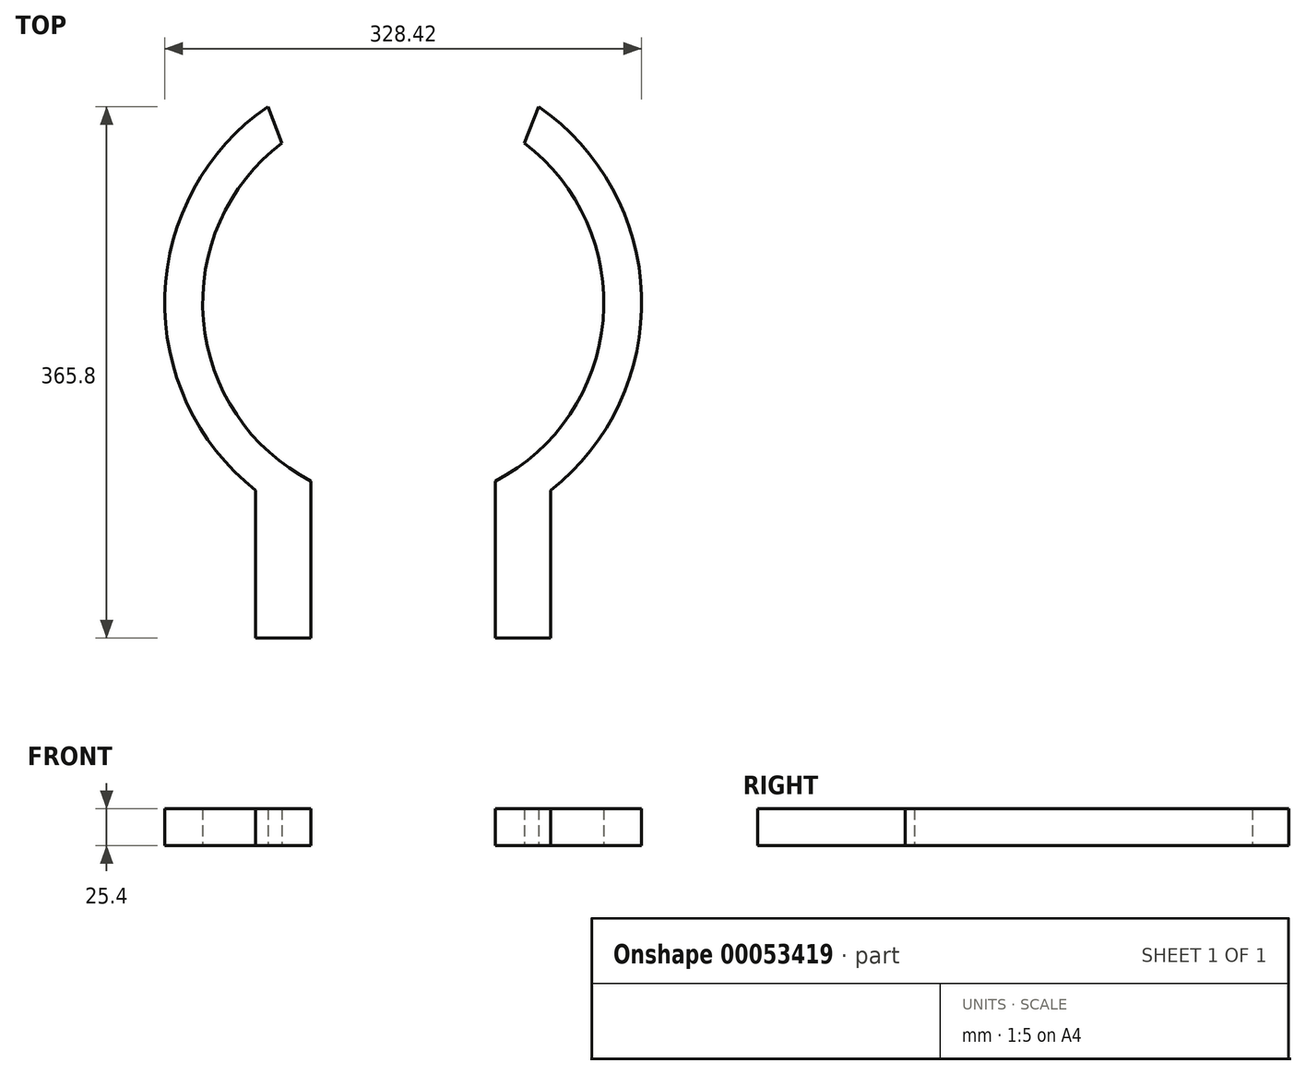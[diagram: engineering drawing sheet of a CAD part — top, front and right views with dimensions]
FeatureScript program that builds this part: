
annotation { "Feature Type Name" : "Feature", "Feature Type Description" : "" }
export const myFeature = defineFeature(function(context is Context, id is Id, definition is map)
    precondition{}
    {
        {
            var Q0;
            Q0=qCreatedBy(makeId("Top.planeOp"),FACE);
            var sketch = newSketch(context, id + "F0", { "sketchPlane" : qUnion([Q0])});
            skLineSegment(sketch, "E0", {"start": v(-63.5, -122.65) * mm, "end": v(-63.5, -230.6) * mm});
            skLineSegment(sketch, "E1", {"start": v(-63.5, -230.6) * mm, "end": v(-101.6, -230.6) * mm});
            skLineSegment(sketch, "E2", {"start": v(-101.6, -230.6) * mm, "end": v(-101.6, -129) * mm});
            skArc(sketch, "E3", {"start": v(-83.53, 110) * mm, "mid": v(-137.6, -11.85) * mm, "end": v(-63.5, -122.65) * mm});
            skArc(sketch, "E4", {"start": v(-93.19, 135.2) * mm, "mid": v(-164.12, 5.22) * mm, "end": v(-101.6, -129) * mm});
            skLineSegment(sketch, "E5", {"start": v(-93.19, 135.2) * mm, "end": v(-83.53, 110) * mm});
            skLineSegment(sketch, "E6.MirrorCS", {"start": v(93.19, 135.2) * mm, "end": v(83.53, 110) * mm});
            skLineSegment(sketch, "E7.MirrorCS", {"start": v(63.5, -230.6) * mm, "end": v(101.6, -230.6) * mm});
            skArc(sketch, "E8.MirrorCS", {"start": v(93.19, 135.2) * mm, "mid": v(164.12, 5.22) * mm, "end": v(101.6, -129) * mm});
            skLineSegment(sketch, "E9.MirrorCS", {"start": v(101.6, -230.6) * mm, "end": v(101.6, -129) * mm});
            skLineSegment(sketch, "E10.MirrorCS", {"start": v(63.5, -122.65) * mm, "end": v(63.5, -230.6) * mm});
            skArc(sketch, "E11.MirrorCS", {"start": v(83.53, 110) * mm, "mid": v(137.6, -11.85) * mm, "end": v(63.5, -122.65) * mm});
            skArc(sketch, "E12", {"start": v(137.78, -9.52) * mm, "mid": v(138.11, 0) * mm, "end": v(137.78, 9.53) * mm});
            skLineSegment(sketch, "E13", {"start": v(137.78, 9.53) * mm, "end": v(163.93, 9.53) * mm});
            skLineSegment(sketch, "E14", {"start": v(163.93, 9.53) * mm, "end": v(163.93, -9.52) * mm});
            skLineSegment(sketch, "E15", {"start": v(163.93, -9.52) * mm, "end": v(137.78, -9.52) * mm});
            skArc(sketch, "E16.MirrorCS", {"start": v(-137.78, -9.52) * mm, "mid": v(-138.11, 0) * mm, "end": v(-137.78, 9.53) * mm});
            skLineSegment(sketch, "E17.MirrorCS", {"start": v(-163.93, -9.52) * mm, "end": v(-137.78, -9.52) * mm});
            skLineSegment(sketch, "E18.MirrorCS", {"start": v(-137.78, 9.53) * mm, "end": v(-163.93, 9.53) * mm});
            skLineSegment(sketch, "E19.MirrorCS", {"start": v(-163.93, 9.53) * mm, "end": v(-163.93, -9.52) * mm});
            skSolve(sketch);
        }
        {
            var Q0;
            Q0=qSketchRegion(id+"F0",true);
            extrude(context, id + "F1", {"entities" : qUnion([Q0]), "depth" : 25.4 * mm});
        }
    });
